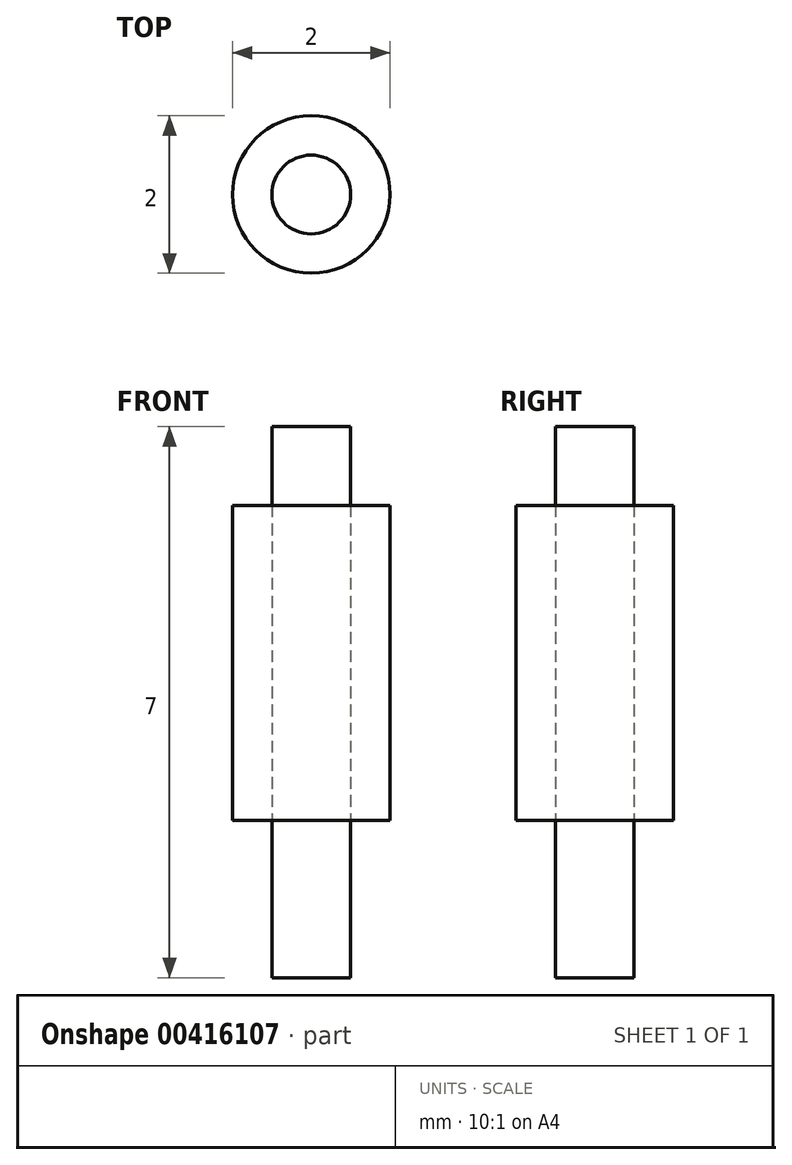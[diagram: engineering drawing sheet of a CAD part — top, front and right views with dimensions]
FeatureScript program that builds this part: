
annotation { "Feature Type Name" : "Feature", "Feature Type Description" : "" }
export const myFeature = defineFeature(function(context is Context, id is Id, definition is map)
    precondition{}
    {
        {
            var Q0;
            Q0=qCreatedBy(makeId("Top.planeOp"),FACE);
            var sketch = newSketch(context, id + "F0", { "sketchPlane" : qUnion([Q0])});
            skCircle(sketch, "E0", {"center": v(0, 0) * mm, "radius": 0.5 * mm});
            skSolve(sketch);
        }
        {
            var Q0;
            Q0=makeQuery(id+"F0.imprint","IMPRINT",FACE,{"disambiguationData":[TD([[makeQuery(id+"F0.imprint","IMPRINT",EDGE,{"derivedFrom":sQuery(id+"F0.wireOp",EDGE,"E0")}),1.0]])]});
            extrude(context, id + "F1", {"entities" : qUnion([Q0]), "depth" : 5 * mm, "hasSecondDirection" : true, "secondDirectionOppositeDirection" : true, "secondDirectionDepth" : 2 * mm});
        }
        {
            var Q0;
            Q0=qCreatedBy(makeId("Top.planeOp"),FACE);
            var sketch = newSketch(context, id + "F2", { "sketchPlane" : qUnion([Q0])});
            skCircle(sketch, "E1", {"center": v(0, 0) * mm, "radius": 1 * mm});
            skSolve(sketch);
        }
        {
            var Q0;
            Q0=makeQuery(id+"F2.imprint","IMPRINT",FACE,{"disambiguationData":[TD([[makeQuery(id+"F2.imprint","IMPRINT",EDGE,{"derivedFrom":sQuery(id+"F2.wireOp",EDGE,"E1")}),1.0]])]});
            extrude(context, id + "F3", {"entities" : qUnion([Q0]), "depth" : 4 * mm});
        }
    });
